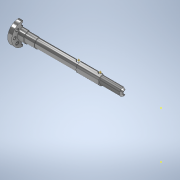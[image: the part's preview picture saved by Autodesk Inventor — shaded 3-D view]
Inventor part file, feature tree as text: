
AUTODESK INVENTOR PART (.ipt)
format: ipt  version: 2022 (Build 260153000, 153)  size: 271,872 bytes
history: native  units: in
note: dims shown in document units (in); Inventor stores cm internally (conversion verified against a paired STEP export)
features: sketch x10, plane x5, extrude x4, other x4, revolve x3, chamfer x3, thread x2
ambient origin geometry x8: Origin, YZ Plane, XZ Plane, XY Plane, X Axis, Y Axis, Z Axis, Center Point
bodies: Solid1 (feature_tree)
feature tree (31):
  revolve  "Revolution1"  [1 undecoded]
  plane  "Work Plane2"
  extrude  "Extrusion1"  Depth=0.8465in
  sketch  "Sketch4"  dims[d12=0.4331in d13=0.3465in]
  extrude  "Extrusion2"  Depth=0.3465in
  sketch  "Sketch6"  dims[d16=0.3819in d17=0.3819in]
  plane  "Work Plane3"
  revolve  "Revolution2"  [1 undecoded]
  revolve  "Revolution3"  [1 undecoded]
  extrude  "Extrusion8"  TaperAngle=90.0deg  [1 undecoded]
  chamfer  "Chamfer1"  Distance=0.1732in
  chamfer  "Chamfer2"  Distance=1.7913in
  plane  "Work Plane5"
  extrude  "Extrusion9"  TaperAngle=90.0deg  [1 undecoded]
  chamfer  "Chamfer3"  Distance=0.8661in
  sketch  "Sketch18"  dims[d39=0.6299in d40=0.8661in d41=120.0deg d42=0.2874in d43=0.315in d44=0.1063in d45=3.1496in d47=360.0deg d49=0.3937in d50=0.0in d51=0.0079in d52=0.0787in d53=45.0deg d54=0.063in d55=0.0787in d56=45.0deg d57=-0.9646in d58=0.0984in d59=0.3937in d60=0.0in d61=0.0197in d62=0.0787in d63=45.0deg d66=0.7835in d67=0.0in d68=0.1098in d69=0.0in]
  thread  "Thread1"  [1 undecoded]
  thread  "Thread2"  [1 undecoded]
  sketch  "Sketch2"  dims[d8=4.1142in d9=3.9567in]
  plane  "Work Plane1"
  other  "Work Axis1"
  other  "Work Point1"
  sketch  "Sketch3"  dims[d10=3.7205in d11=0.8465in]
  sketch  "Sketch5"  dims[d14=3.3268in d15=1.7126in]
  sketch  "Sketch10"  dims[d18=0.315in d19=90.0deg]
  sketch  "Sketch14"  dims[d20=-1.7913in d21=0.1732in d22=0.0in d23=1.7913in d24=0.0in]
  sketch  "Sketch15"  dims[d26=90.0deg d37=90.0deg]
  plane  "Work Plane4"
  other  "Work Axis2"
  other  "Work Point2"
  sketch  "Sketch16"  dims[d38=90.0deg]
note: 7 required parameter values undecoded (feature->parameter linkage not recoverable at this tier; creation-order binding heuristic only, values carry confidence <= 0.55)